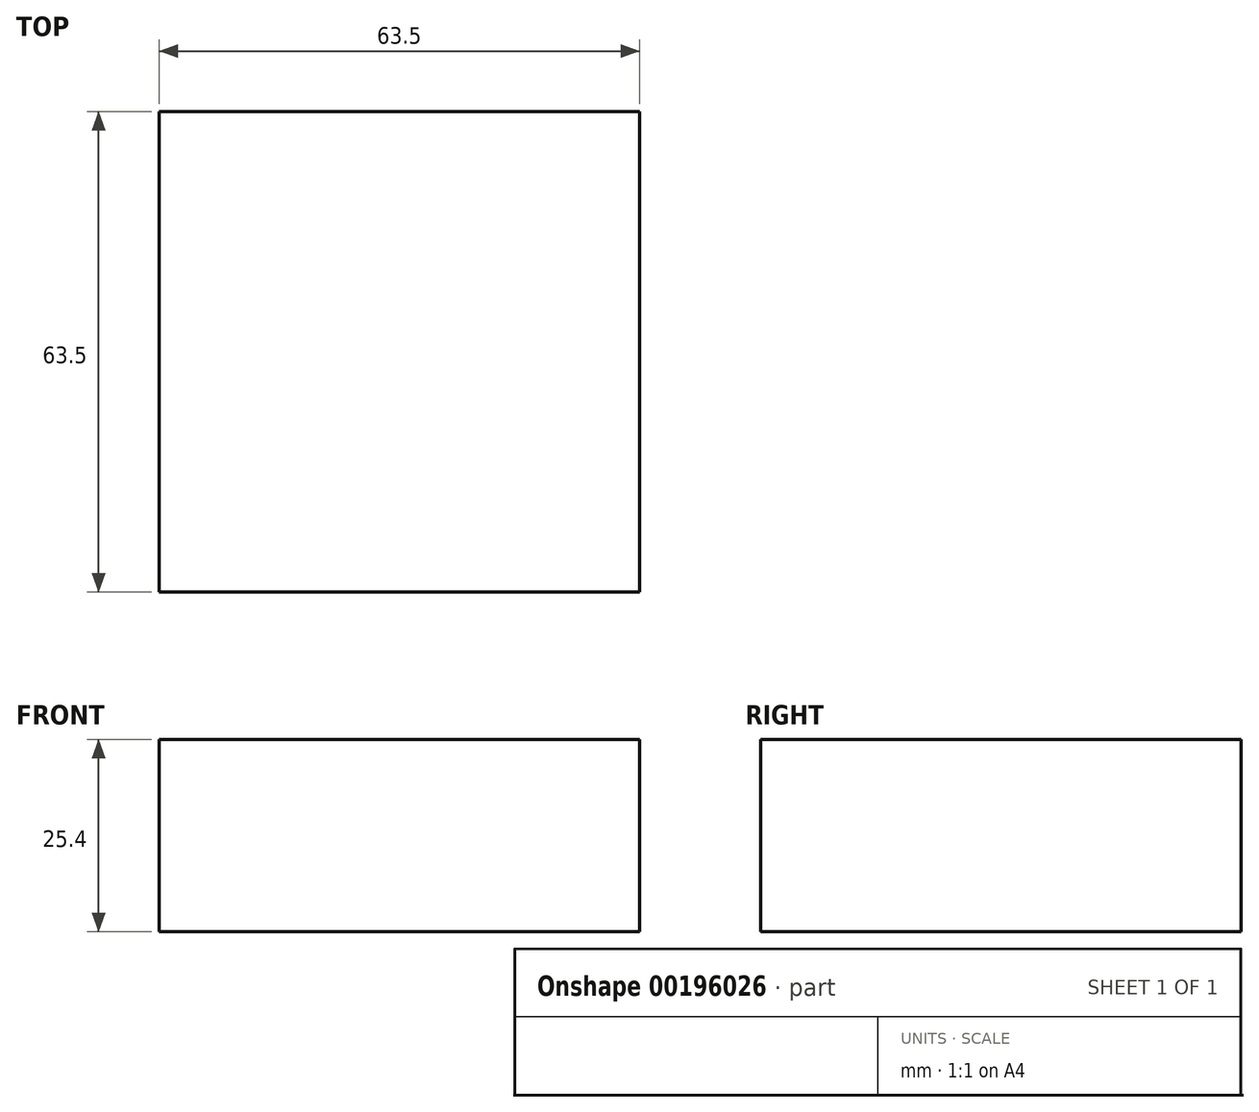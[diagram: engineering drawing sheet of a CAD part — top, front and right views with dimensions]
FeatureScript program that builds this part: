
annotation { "Feature Type Name" : "Feature", "Feature Type Description" : "" }
export const myFeature = defineFeature(function(context is Context, id is Id, definition is map)
    precondition{}
    {
        {
            var Q0;
            Q0=qCreatedBy(makeId("Top.planeOp"),FACE);
            var sketch = newSketch(context, id + "F0", { "sketchPlane" : qUnion([Q0])});
            skLineSegment(sketch, "E0.bottom", {"start": v(-31.75, 29.77) * mm, "end": v(31.75, 29.77) * mm});
            skLineSegment(sketch, "E0.top", {"start": v(-31.75, -33.73) * mm, "end": v(31.75, -33.73) * mm});
            skLineSegment(sketch, "E0.left", {"start": v(-31.75, 29.77) * mm, "end": v(-31.75, -33.73) * mm});
            skLineSegment(sketch, "E0.right", {"start": v(31.75, 29.77) * mm, "end": v(31.75, -33.73) * mm});
            skSolve(sketch);
        }
        {
            var Q0;
            Q0 = qSketchRegion(id + "F0", true);
            extrude(context, id + "F1", {"entities" : qUnion([Q0]), "depth" : 25.4 * mm});
        }
    });
